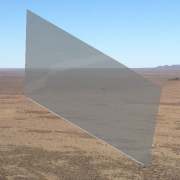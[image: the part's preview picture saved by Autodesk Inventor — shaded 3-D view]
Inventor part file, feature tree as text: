
AUTODESK INVENTOR PART (.ipt)
format: ipt  version: 2013 SP2 (Build 170200200, 200)  size: 151,040 bytes
history: native  units: in
note: dims shown in document units (in); Inventor stores cm internally (conversion verified against a paired STEP export)
features: extrude x4, sketch x4, plane x1
ambient origin geometry x8: Origin, YZ Plane, XZ Plane, XY Plane, X Axis, Y Axis, Z Axis, Center Point
bodies: Solid1 (feature_tree)
feature tree (9):
  extrude  "bottomMateSurface"  Depth=1.0in
  plane  "Work Plane1"
  extrude  "centralPanelPortion"  Depth=0.0481in
  extrude  "extensionRight"  Depth=0.25in
  extrude  "extensionLeft"  Depth=4.0in
  sketch  "Sketch1"  dims[d0=136.0in d1=1.0in]
  sketch  "Sketch2"  dims[d2=0.25in d3=0.0in d4=0.0481in]
  sketch  "Sketch5"  dims[d5=136.0in d6=0.25in]
  sketch  "Sketch6"  dims[d7=80.0in d8=0.0in d16=4.0in d17=11.0in d18=0.25in d19=0.0in d20=4.0in d21=11.0in d22=0.25in d23=0.0in]
